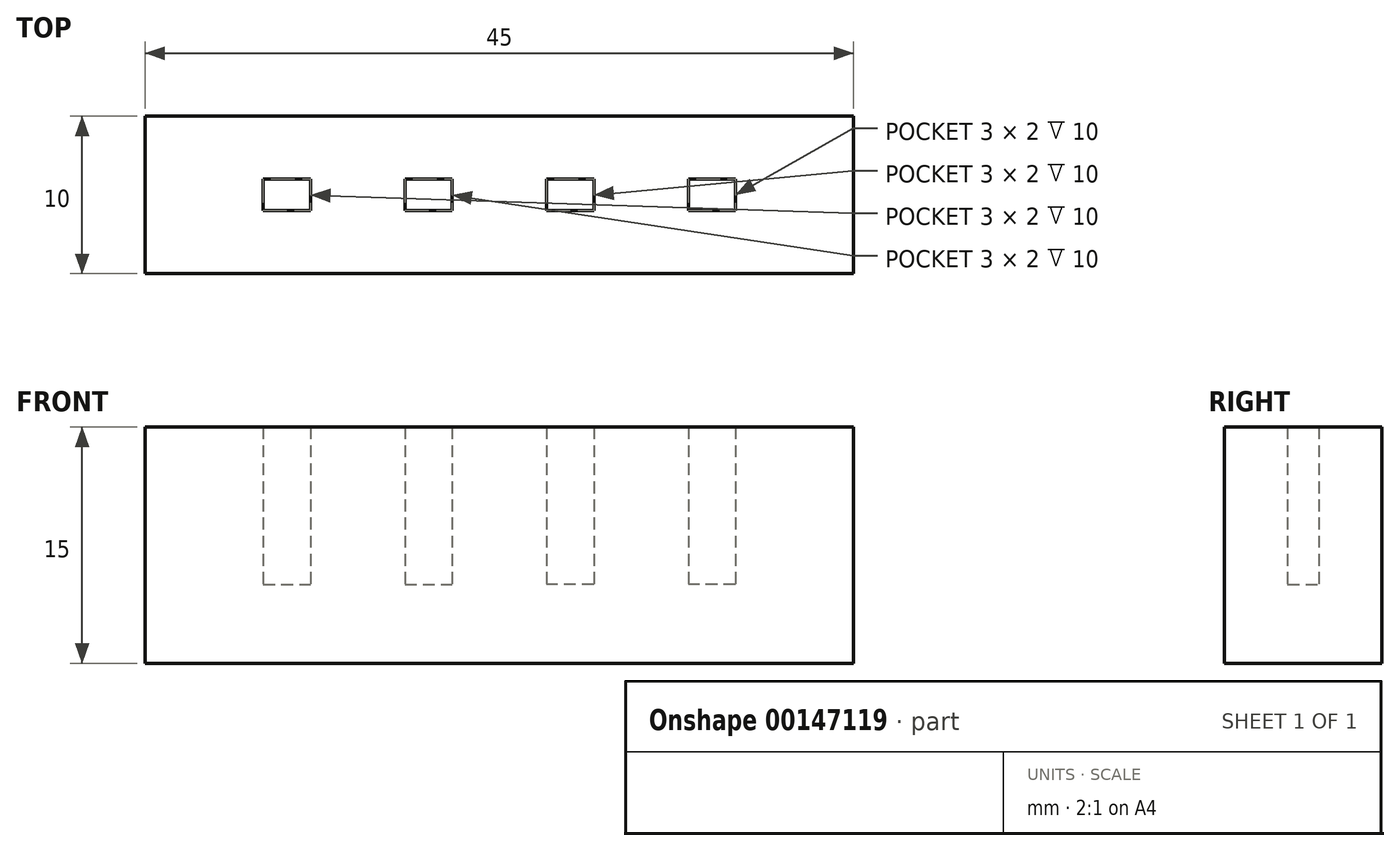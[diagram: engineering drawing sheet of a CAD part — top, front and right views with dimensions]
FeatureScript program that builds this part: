
annotation { "Feature Type Name" : "Feature", "Feature Type Description" : "" }
export const myFeature = defineFeature(function(context is Context, id is Id, definition is map)
    precondition{}
    {
        {
            var Q0;
            Q0=qCreatedBy(makeId("Top.planeOp"),FACE);
            var sketch = newSketch(context, id + "F0", { "sketchPlane" : qUnion([Q0])});
            skLineSegment(sketch, "E0.bottom", {"start": v(-22.5, 5) * mm, "end": v(22.5, 5) * mm});
            skLineSegment(sketch, "E0.top", {"start": v(-22.5, -5) * mm, "end": v(22.5, -5) * mm});
            skLineSegment(sketch, "E0.left", {"start": v(-22.5, 5) * mm, "end": v(-22.5, -5) * mm});
            skLineSegment(sketch, "E0.right", {"start": v(22.5, 5) * mm, "end": v(22.5, -5) * mm});
            skPoint(sketch, "E0.middle", {"position": v(0, 0) * mm});
            skLineSegment(sketch, "E1", {"start": v(0, 0) * mm, "end": v(4.5, 0) * mm});
            skLineSegment(sketch, "E2", {"start": v(4.5, 0) * mm, "end": v(13.5, 0) * mm});
            skLineSegment(sketch, "E3.bottom", {"start": v(15, -1) * mm, "end": v(12, -1) * mm});
            skLineSegment(sketch, "E3.top", {"start": v(15, 1) * mm, "end": v(12, 1) * mm});
            skLineSegment(sketch, "E3.left", {"start": v(15, -1) * mm, "end": v(15, 1) * mm});
            skLineSegment(sketch, "E3.right", {"start": v(12, -1) * mm, "end": v(12, 1) * mm});
            skPoint(sketch, "E3.middle", {"position": v(13.5, 0) * mm});
            skLineSegment(sketch, "E4.bottom", {"start": v(6, 1) * mm, "end": v(3, 1) * mm});
            skLineSegment(sketch, "E4.top", {"start": v(6, -1) * mm, "end": v(3, -1) * mm});
            skLineSegment(sketch, "E4.left", {"start": v(6, 1) * mm, "end": v(6, -1) * mm});
            skLineSegment(sketch, "E4.right", {"start": v(3, 1) * mm, "end": v(3, -1) * mm});
            skPoint(sketch, "E4.middle", {"position": v(4.5, 0) * mm});
            skLineSegment(sketch, "E5.MirrorCS", {"start": v(-15, -1) * mm, "end": v(-12, -1) * mm});
            skLineSegment(sketch, "E6.MirrorCS", {"start": v(-15, 1) * mm, "end": v(-12, 1) * mm});
            skLineSegment(sketch, "E7.MirrorCS", {"start": v(-12, -1) * mm, "end": v(-12, 1) * mm});
            skLineSegment(sketch, "E8.MirrorCS", {"start": v(-15, -1) * mm, "end": v(-15, 1) * mm});
            skLineSegment(sketch, "E9.MirrorCS", {"start": v(-6, 1) * mm, "end": v(-3, 1) * mm});
            skLineSegment(sketch, "E10.MirrorCS", {"start": v(-6, 1) * mm, "end": v(-6, -1) * mm});
            skLineSegment(sketch, "E11.MirrorCS", {"start": v(-6, -1) * mm, "end": v(-3, -1) * mm});
            skLineSegment(sketch, "E12.MirrorCS", {"start": v(-3, 1) * mm, "end": v(-3, -1) * mm});
            skSolve(sketch);
        }
        {
            var Q0;
            Q0=makeQuery(id+"F0.imprint","IMPRINT",FACE,{"disambiguationData":[TD([[makeQuery(id+"F0.imprint","IMPRINT",EDGE,{"derivedFrom":sQuery(id+"F0.wireOp",EDGE,"E0.bottom")}),-1.0]])]});
            extrude(context, id + "F1", {"entities" : qUnion([Q0]), "depth" : 15 * mm});
        }
        {
            var Q0;
            Q0=makeQuery(id+"F0.imprint","IMPRINT",FACE,{"disambiguationData":[TD([[makeQuery(id+"F0.imprint","IMPRINT",EDGE,{"derivedFrom":sQuery(id+"F0.wireOp",EDGE,"E5.MirrorCS")}),1.0]])]});
            var Q1;
            Q1=makeQuery(id+"F0.imprint","IMPRINT",FACE,{"disambiguationData":[TD([[makeQuery(id+"F0.imprint","IMPRINT",EDGE,{"derivedFrom":sQuery(id+"F0.wireOp",EDGE,"E9.MirrorCS")}),-1.0]])]});
            var Q2;
            {var subQ1=sQuery(id+"F0.wireOp",EDGE,"E4.bottom");Q2=makeQuery(id+"F0.imprint","IMPRINT",FACE,{"disambiguationData":[TD([[makeQuery(id+"F0.imprint","IMPRINT",EDGE,{"derivedFrom":subQ1}),1.0]])]});}
            var Q3;
            {var subQ1=sQuery(id+"F0.wireOp",EDGE,"E4.top");Q3=makeQuery(id+"F0.imprint","IMPRINT",FACE,{"disambiguationData":[TD([[makeQuery(id+"F0.imprint","IMPRINT",EDGE,{"derivedFrom":subQ1}),-1.0]])]});}
            var Q4;
            {var subQ1=sQuery(id+"F0.wireOp",EDGE,"E3.bottom");Q4=makeQuery(id+"F0.imprint","IMPRINT",FACE,{"disambiguationData":[TD([[makeQuery(id+"F0.imprint","IMPRINT",EDGE,{"derivedFrom":subQ1}),-1.0]])]});}
            extrude(context, id + "F2", {"entities" : qUnion([Q0, Q1, Q2, Q3, Q4]), "operationType" : NewBodyOperationType.ADD, "depth" : 5 * mm});
        }
    });
